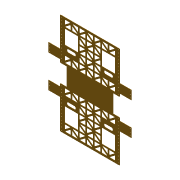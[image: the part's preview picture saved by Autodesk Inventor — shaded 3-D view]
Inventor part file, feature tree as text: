
AUTODESK INVENTOR PART (.ipt)
format: ipt  version: 2015 (Build 190159000, 159)  size: 2,122,752 bytes
history: native  units: in
note: dims shown in document units (in); Inventor stores cm internally (conversion verified against a paired STEP export)
features: sketch x7, extrude x6, hole x1, fillet x1, projected_geometry x1
ambient origin geometry x8: Origin, YZ Plane, XZ Plane, XY Plane, X Axis, Y Axis, Z Axis, Center Point
bodies: Solid1 (feature_tree)
feature tree (16):
  extrude  "Extrusion1"  Depth=20.0in
  hole  "Hole1"  [1 undecoded]
  extrude  "Extrusion2"  Depth=0.09in TaperAngle=0.0deg
  extrude  "Extrusion4"  Depth=0.5in
  extrude  "Extrusion5"  Depth=0.5in
  extrude  "Extrusion6"  Depth=0.5in
  extrude  "Extrusion7"  Depth=6.0in
  fillet  "Fillet1"  Radius=2.25in
  sketch  "Sketch1"  dims[d0=4.0in d1=20.0in]
  sketch  "Sketch2"  dims[d2=10.0in d3=3.0in]
  sketch  "Sketch4"  dims[d4=8.0in d5=0.09in d6=0.0in]
  sketch  "Sketch6"  dims[d7=0.5in d8=0.5in]
  projected_geometry  "Projected Loop2"
  sketch  "Sketch7"  dims[d9=0.5in d10=0.5in]
  sketch  "Sketch8"  dims[d11=13.3858in d13=1.0in d14=0.3937in d16=1.0in d18=0.5in]
  sketch  "Sketch9"  dims[d19=0.5in d20=0.266in d21=0.75in d22=0.375in d23=0.25in d24=0.5635in d25=1.0in d26=0.8108in d27=6.0in d28=2.25in d29=2.25in d30=6.0in d31=1.0in d32=1.0in d33=0.09in d34=0.0in d38=2.0in d96=18.0in d97=11.0in d181=2.0in d182=1.5in d184=0.5in d185=0.125in d186=0.25in d187=0.25in d188=1.5in d189=0.6875in d190=2.0in d191=1.5in d192=0.5in d193=0.125in d194=0.25in d195=0.25in d196=0.5in d197=2.0in d198=1.5in d199=0.5in d200=0.125in d201=0.25in d202=0.25in d203=2.0in d204=1.5in d205=0.5in d206=0.125in d207=0.5in d208=0.5in d209=0.5in d210=1.5in d211=2.0in d212=1.5in d213=0.5in d214=0.125in d215=0.25in d216=0.25in d217=2.0in d218=1.5in d219=0.5in d220=0.125in d221=0.25in d222=0.25in d223=0.5in d224=2.0in d225=1.5in d226=0.5in d227=0.125in d228=0.25in d229=0.25in d230=2.0in d231=1.5in d232=0.5in d233=0.125in d234=0.5in d235=0.5in d236=0.5in d237=0.5in d238=2.0in d239=1.5in d240=0.5in d241=0.125in d242=0.25in d244=2.0in d245=1.5in d246=0.5in d247=0.125in d248=0.25in d250=0.5in d251=2.0in d252=1.5in d253=0.5in d254=0.125in d255=0.25in d257=2.0in d258=1.5in d259=0.5in d260=0.125in d261=0.5in d263=0.5in d264=0.5in d265=0.6875in d266=2.0in d267=1.5in d268=0.5in d269=0.125in d270=0.25in d271=0.25in d274=2.0in d275=1.5in d276=0.5in d277=0.125in d278=0.25in d279=0.25in d280=0.5in d281=2.0in d282=1.5in d283=0.5in d284=0.125in d285=0.25in d286=0.25in d287=2.0in d288=1.5in d289=0.5in d290=0.125in d291=0.5in d292=0.5in d293=0.5in d295=2.0in d296=1.5in d297=0.5in d298=0.125in d299=0.25in d300=0.25in d301=2.0in d302=1.5in d303=0.5in d304=0.125in d305=0.25in d306=0.25in d307=0.5in d308=2.0in d309=1.5in d310=0.5in d311=0.125in d312=0.25in d313=0.25in d314=2.0in d315=1.5in d316=0.5in d317=0.125in d318=0.5in d319=0.5in d320=0.5in d321=0.5in d322=2.0in d323=1.5in d324=0.5in d325=0.125in d326=0.25in d327=2.0in d328=1.5in d329=0.5in d330=0.125in d331=0.25in d332=0.5in d333=2.0in d334=1.5in d335=0.5in d336=0.125in d337=0.25in d338=2.0in d339=1.5in d340=0.5in d341=0.125in d342=0.5in d343=0.5in d344=0.5in d346=0.6875in d347=1.0in d348=0.0in d349=0.0in d350=0.0in d351=0.0in d352=0.0in d353=0.0in d354=0.0in d355=0.0in d356=0.0in d357=0.125in d358=0.0in d359=0.0in d360=0.0in d361=0.0in d362=0.0in d363=0.0in d364=0.0in d365=0.0in d366=0.125in d367=1.0in d368=0.0in d369=0.09in d370=0.0in d371=2.0in d372=2.25in d373=1.0in d374=1.1875in d375=0.09in d376=0.0in d377=0.125in]
note: 1 required parameter value undecoded (feature->parameter linkage not recoverable at this tier; creation-order binding heuristic only, values carry confidence <= 0.55)
